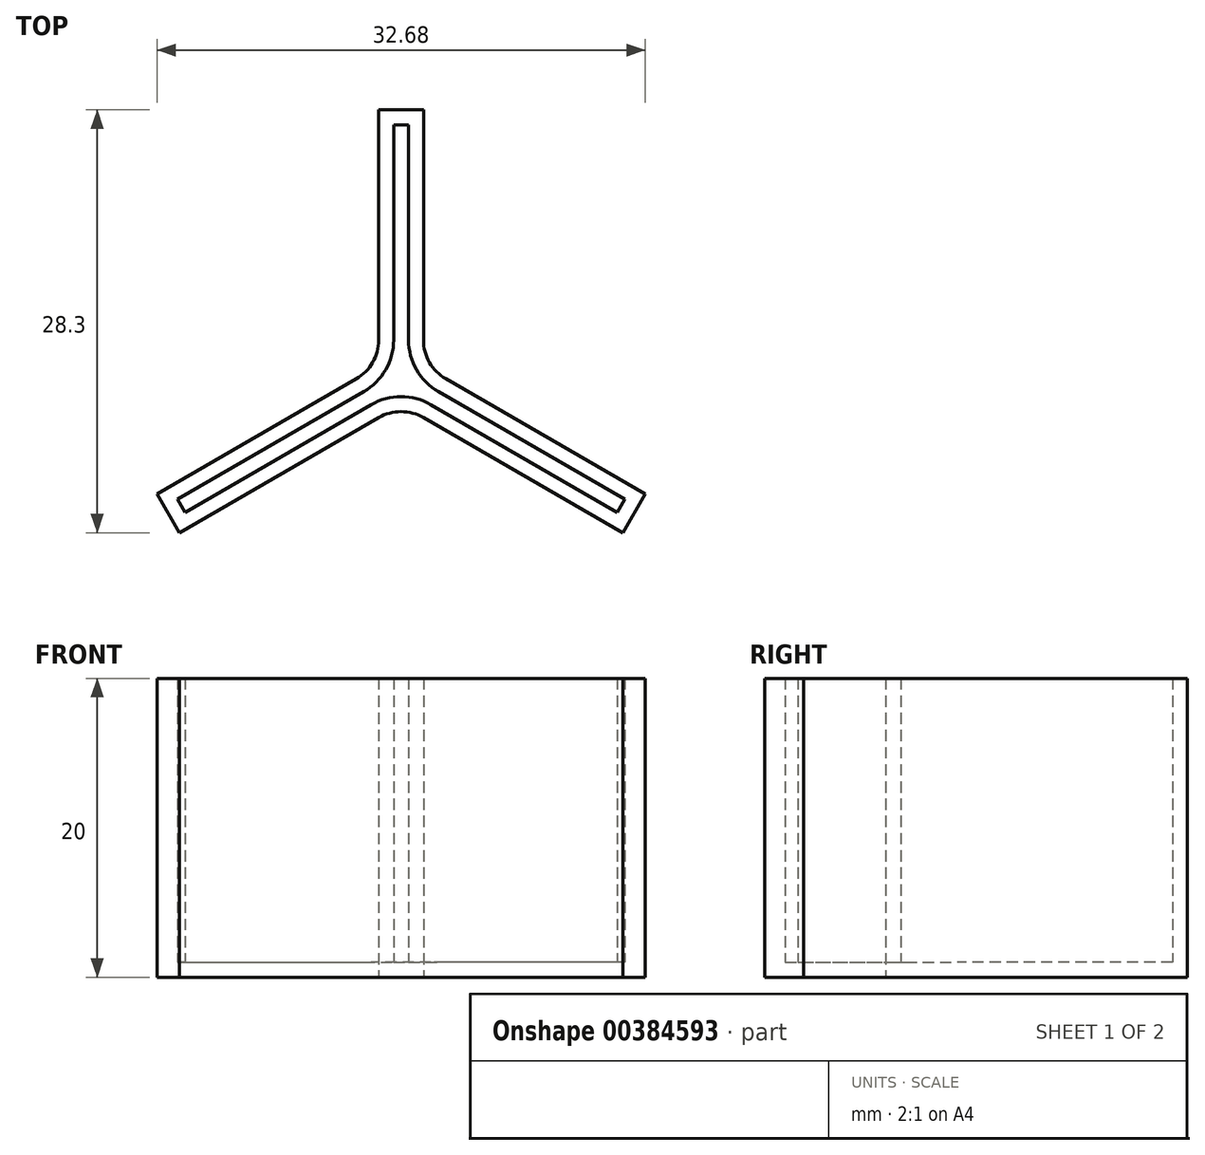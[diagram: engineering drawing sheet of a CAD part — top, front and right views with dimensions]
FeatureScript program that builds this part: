
annotation { "Feature Type Name" : "Feature", "Feature Type Description" : "" }
export const myFeature = defineFeature(function(context is Context, id is Id, definition is map)
    precondition{}
    {
        {
            var Q0;
            Q0=qCreatedBy(makeId("Top.planeOp"),FACE);
            var sketch = newSketch(context, id + "F0", { "sketchPlane" : qUnion([Q0])});
            skLineSegment(sketch, "E0", {"start": v(-0.5, 17) * mm, "end": v(0.5, 17) * mm});
            skLineSegment(sketch, "E1", {"start": v(0.5, 17) * mm, "end": v(0.5, 2.3) * mm});
            skLineSegment(sketch, "E2.MirrorCS", {"start": v(-0.5, 17) * mm, "end": v(-0.5, 2.3) * mm});
            skLineSegment(sketch, "E3.2.0", {"start": v(-1.5, 18) * mm, "end": v(-1.5, 2.6) * mm});
            skLineSegment(sketch, "E3.2.1", {"start": v(-1.5, 18) * mm, "end": v(1.5, 18) * mm});
            skLineSegment(sketch, "E3.2.2", {"start": v(1.5, 18) * mm, "end": v(1.5, 2.6) * mm});
            skLineSegment(sketch, "E4.1.0", {"start": v(-14.97, -8.07) * mm, "end": v(-2.25, -0.72) * mm});
            skLineSegment(sketch, "E4.1.1", {"start": v(-16.34, -7.7) * mm, "end": v(-3, 0) * mm});
            skLineSegment(sketch, "E4.1.2", {"start": v(-14.84, -10.3) * mm, "end": v(-16.34, -7.7) * mm});
            skLineSegment(sketch, "E4.1.3", {"start": v(-14.84, -10.3) * mm, "end": v(-1.5, -2.6) * mm});
            skLineSegment(sketch, "E4.1.4", {"start": v(-14.47, -8.93) * mm, "end": v(-1.75, -1.59) * mm});
            skLineSegment(sketch, "E4.1.5", {"start": v(-14.47, -8.93) * mm, "end": v(-14.97, -8.07) * mm});
            skLineSegment(sketch, "E4.2.0", {"start": v(14.47, -8.93) * mm, "end": v(1.75, -1.59) * mm});
            skLineSegment(sketch, "E4.2.1", {"start": v(14.84, -10.3) * mm, "end": v(1.5, -2.6) * mm});
            skLineSegment(sketch, "E4.2.2", {"start": v(16.34, -7.7) * mm, "end": v(14.84, -10.3) * mm});
            skLineSegment(sketch, "E4.2.3", {"start": v(16.34, -7.7) * mm, "end": v(3, 0) * mm});
            skLineSegment(sketch, "E4.2.4", {"start": v(14.97, -8.07) * mm, "end": v(2.25, -0.72) * mm});
            skLineSegment(sketch, "E4.2.5", {"start": v(14.97, -8.07) * mm, "end": v(14.47, -8.93) * mm});
            skPoint(sketch, "E4.center", {"position": v(0, 0) * mm});
            skPoint(sketch, "E5.newPointA", {"position": v(2.75, 0.14) * mm});
            skPoint(sketch, "E5.newPointB", {"position": v(1.5, 2.3) * mm});
            skArc(sketch, "E5.filletArc", {"start": v(1.5, 2.6) * mm, "mid": v(1.9, 1.1) * mm, "end": v(3, 0) * mm});
            skPoint(sketch, "E6.newPointA", {"position": v(-2.75, 0.14) * mm});
            skPoint(sketch, "E6.newPointB", {"position": v(-1.5, 2.3) * mm});
            skArc(sketch, "E6.filletArc", {"start": v(-3, 0) * mm, "mid": v(-1.9, 1.1) * mm, "end": v(-1.5, 2.6) * mm});
            skPoint(sketch, "E7.newPointA", {"position": v(-1.25, -2.45) * mm});
            skPoint(sketch, "E7.newPointB", {"position": v(1.25, -2.45) * mm});
            skArc(sketch, "E7.filletArc", {"start": v(1.5, -2.6) * mm, "mid": v(0, -2.2) * mm, "end": v(-1.5, -2.6) * mm});
            skArc(sketch, "E8.0", {"start": v(2, -1.73) * mm, "mid": v(0, -1.2) * mm, "end": v(-2, -1.73) * mm});
            skArc(sketch, "E9.0", {"start": v(0.5, 2.6) * mm, "mid": v(1.04, 0.6) * mm, "end": v(2.5, -0.87) * mm});
            skArc(sketch, "E10.0", {"start": v(-2.5, -0.87) * mm, "mid": v(-1.04, 0.6) * mm, "end": v(-0.5, 2.6) * mm});
            skSolve(sketch);
        }
        {
            var Q0;
            Q0=qSketchRegion(id+"F0",true);
            extrude(context, id + "F1", {"entities" : qUnion([Q0]), "depth" : 20 * mm});
        }
        {
            var Q0;
            Q0=makeQuery(id+"F1.opExtrude","CAP_FACE",FACE,{"disambiguationData":[OSD([sQuery(id+"F0.wireOp",EDGE,"E0"),sQuery(id+"F0.wireOp",EDGE,"E1"),sQuery(id+"F0.wireOp",EDGE,"E2.MirrorCS"),sQuery(id+"F0.wireOp",EDGE,"337185be-f85e-4477-9048-b1e5cd72ba38.1.0"),sQuery(id+"F0.wireOp",EDGE,"337185be-f85e-4477-9048-b1e5cd72ba38.1.1"),sQuery(id+"F0.wireOp",EDGE,"337185be-f85e-4477-9048-b1e5cd72ba38.1.2"),sQuery(id+"F0.wireOp",EDGE,"337185be-f85e-4477-9048-b1e5cd72ba38.2.0"),sQuery(id+"F0.wireOp",EDGE,"337185be-f85e-4477-9048-b1e5cd72ba38.2.1"),sQuery(id+"F0.wireOp",EDGE,"337185be-f85e-4477-9048-b1e5cd72ba38.2.2"),sQuery(id+"F0.wireOp",EDGE,"10e7eb02-b686-412f-9961-15af4ba6b5a4.0"),sQuery(id+"F0.wireOp",EDGE,"584127d9-0715-4318-be33-4c08fe5fe5c3.0"),sQuery(id+"F0.wireOp",EDGE,"2b1b5de7-14f9-4f3f-9905-628b27bdaed7.0"),sQuery(id+"F0.wireOp",EDGE,"3dd13835-8f9a-4838-b6b1-501ea5813092.1.0"),sQuery(id+"F0.wireOp",EDGE,"3dd13835-8f9a-4838-b6b1-501ea5813092.1.1"),sQuery(id+"F0.wireOp",EDGE,"3dd13835-8f9a-4838-b6b1-501ea5813092.1.2"),sQuery(id+"F0.wireOp",EDGE,"3dd13835-8f9a-4838-b6b1-501ea5813092.2.0"),sQuery(id+"F0.wireOp",EDGE,"3dd13835-8f9a-4838-b6b1-501ea5813092.2.1"),sQuery(id+"F0.wireOp",EDGE,"3dd13835-8f9a-4838-b6b1-501ea5813092.2.2")])],"isStart":true});
            var sketch = newSketch(context, id + "F2", { "sketchPlane" : qUnion([Q0])});
            skLineSegment(sketch, "E11.0", {"start": v(-0.5, -17) * mm, "end": v(0.5, -17) * mm});
            skLineSegment(sketch, "E12.0", {"start": v(0.5, -17) * mm, "end": v(0.5, -2.6) * mm});
            skLineSegment(sketch, "E13.0", {"start": v(-0.5, -17) * mm, "end": v(-0.5, -2.6) * mm});
            skArc(sketch, "E14.0", {"start": v(-2.5, 0.87) * mm, "mid": v(-1.04, -0.6) * mm, "end": v(-0.5, -2.6) * mm});
            skLineSegment(sketch, "E15.1.0", {"start": v(14.47, 8.93) * mm, "end": v(2, 1.73) * mm});
            skLineSegment(sketch, "E15.1.1", {"start": v(14.97, 8.07) * mm, "end": v(2.5, 0.87) * mm});
            skArc(sketch, "E15.1.2", {"start": v(0.5, -2.6) * mm, "mid": v(1.04, -0.6) * mm, "end": v(2.5, 0.87) * mm});
            skLineSegment(sketch, "E15.1.3", {"start": v(14.97, 8.07) * mm, "end": v(14.47, 8.93) * mm});
            skLineSegment(sketch, "E15.2.0", {"start": v(-14.97, 8.07) * mm, "end": v(-2.5, 0.87) * mm});
            skLineSegment(sketch, "E15.2.1", {"start": v(-14.47, 8.93) * mm, "end": v(-2, 1.73) * mm});
            skArc(sketch, "E15.2.2", {"start": v(2, 1.73) * mm, "mid": v(0, 1.2) * mm, "end": v(-2, 1.73) * mm});
            skLineSegment(sketch, "E15.2.3", {"start": v(-14.47, 8.93) * mm, "end": v(-14.97, 8.07) * mm});
            skPoint(sketch, "E15.center", {"position": v(0, 0) * mm});
            skSolve(sketch);
        }
        {
            var Q0;
            Q0=qSketchRegion(id+"F2",true);
            extrude(context, id + "F3", {"entities" : qUnion([Q0]), "operationType" : NewBodyOperationType.ADD, "oppositeDirection" : true, "depth" : 1 * mm});
        }
    });
